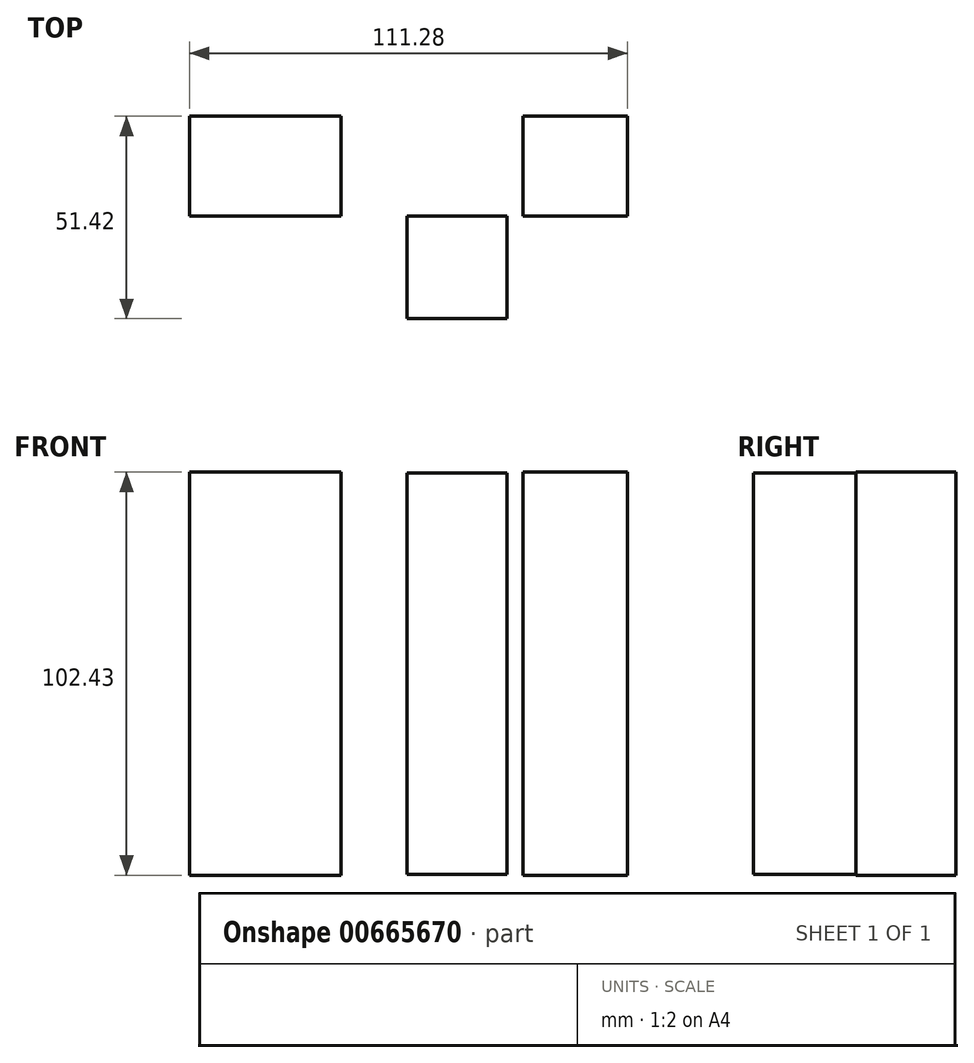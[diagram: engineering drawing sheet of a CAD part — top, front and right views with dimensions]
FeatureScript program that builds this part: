
annotation { "Feature Type Name" : "Feature", "Feature Type Description" : "" }
export const myFeature = defineFeature(function(context is Context, id is Id, definition is map)
    precondition{}
    {
        {
            var Q0;
            Q0=qCreatedBy(makeId("Front.planeOp"),FACE);
            var sketch = newSketch(context, id + "F0", { "sketchPlane" : qUnion([Q0])});
            skLineSegment(sketch, "E0", {"start": v(-55.23, 46.38) * mm, "end": v(-55.23, -56.05) * mm});
            skLineSegment(sketch, "E1", {"start": v(-55.23, -56.05) * mm, "end": v(56.05, -56.05) * mm});
            skLineSegment(sketch, "E2", {"start": v(56.05, -56.05) * mm, "end": v(56.05, 46.38) * mm});
            skLineSegment(sketch, "E3", {"start": v(56.05, 46.38) * mm, "end": v(-55.23, 46.38) * mm});
            skSolve(sketch);
        }
        {
            var Q0;
            Q0 = qSketchRegion(id + "F0", true);
            extrude(context, id + "F1", {"entities" : qUnion([Q0]), "oppositeDirection" : true, "depth" : 25.4 * mm, "offsetDistance" : 25.4 * mm});
        }
        {
            var Q0;
            Q0=qCreatedBy(makeId("Right.planeOp"),FACE);
            var sketch = newSketch(context, id + "F2", { "sketchPlane" : qUnion([Q0])});
            skLineSegment(sketch, "E4", {"start": v(0, 46.18) * mm, "end": v(-26.02, 46.18) * mm});
            skLineSegment(sketch, "E5", {"start": v(-26.02, 46.18) * mm, "end": v(-26.02, -55.84) * mm});
            skLineSegment(sketch, "E6", {"start": v(-26.02, -55.84) * mm, "end": v(0, -55.84) * mm});
            skLineSegment(sketch, "E7", {"start": v(0, -55.84) * mm, "end": v(0, 46.18) * mm});
            skSolve(sketch);
        }
        {
            var Q0;
            Q0 = qSketchRegion(id + "F2", true);
            extrude(context, id + "F3", {"entities" : qUnion([Q0]), "operationType" : NewBodyOperationType.ADD, "depth" : 25.4 * mm, "offsetDistance" : 25.4 * mm});
        }
        {
            var Q0;
            Q0=makeQuery(id+"F1.opExtrude","CAP_FACE",FACE,{"disambiguationData":[OSD([sQuery(id+"F0.wireOp",EDGE,"E0"),sQuery(id+"F0.wireOp",EDGE,"E1"),sQuery(id+"F0.wireOp",EDGE,"E2"),sQuery(id+"F0.wireOp",EDGE,"E3")])],"isStart":false});
            var sketch = newSketch(context, id + "F4", { "sketchPlane" : qUnion([Q0])});
            skLineSegment(sketch, "E8.bottom", {"start": v(-9.15, -56.05) * mm, "end": v(16.76, -56.05) * mm});
            skLineSegment(sketch, "E8.top", {"start": v(-9.15, 46.38) * mm, "end": v(16.76, 46.38) * mm});
            skLineSegment(sketch, "E8.left", {"start": v(-9.15, -56.05) * mm, "end": v(-9.15, 46.38) * mm});
            skLineSegment(sketch, "E8.right", {"start": v(16.76, -56.05) * mm, "end": v(16.76, 46.38) * mm});
            skLineSegment(sketch, "E9.bottom", {"start": v(-9.15, 43.7) * mm, "end": v(-29.52, 43.7) * mm});
            skLineSegment(sketch, "E9.top", {"start": v(-9.15, -56.05) * mm, "end": v(-29.52, -56.05) * mm});
            skLineSegment(sketch, "E9.left", {"start": v(-9.15, 43.7) * mm, "end": v(-9.15, -56.05) * mm});
            skLineSegment(sketch, "E9.right", {"start": v(-29.52, 43.7) * mm, "end": v(-29.52, -56.05) * mm});
            skLineSegment(sketch, "E10.bottom", {"start": v(-29.52, 43.7) * mm, "end": v(-29.52, 43.7) * mm});
            skLineSegment(sketch, "E10.top", {"start": v(-29.52, 46.38) * mm, "end": v(-29.52, 46.38) * mm});
            skLineSegment(sketch, "E10.left", {"start": v(-29.52, 43.7) * mm, "end": v(-29.52, 46.38) * mm});
            skLineSegment(sketch, "E10.right", {"start": v(-29.52, 43.7) * mm, "end": v(-29.52, 46.38) * mm});
            skLineSegment(sketch, "E11.bottom", {"start": v(-29.52, 46.38) * mm, "end": v(16.76, 46.38) * mm});
            skLineSegment(sketch, "E11.top", {"start": v(-29.52, 43.7) * mm, "end": v(16.76, 43.7) * mm});
            skLineSegment(sketch, "E11.left", {"start": v(-29.52, 46.38) * mm, "end": v(-29.52, 43.7) * mm});
            skLineSegment(sketch, "E11.right", {"start": v(16.76, 46.38) * mm, "end": v(16.76, 43.7) * mm});
            skLineSegment(sketch, "E12.bottom", {"start": v(16.76, 43.7) * mm, "end": v(-29.52, 43.7) * mm});
            skLineSegment(sketch, "E12.top", {"start": v(16.76, 21.08) * mm, "end": v(-29.52, 21.08) * mm});
            skLineSegment(sketch, "E12.left", {"start": v(16.76, 43.7) * mm, "end": v(16.76, 21.08) * mm});
            skLineSegment(sketch, "E12.right", {"start": v(-29.52, 43.7) * mm, "end": v(-29.52, 21.08) * mm});
            skSolve(sketch);
        }
        {
            var Q0;
            Q0 = qSketchRegion(id + "F4", true);
            extrude(context, id + "F5", {"entities" : qUnion([Q0]), "operationType" : NewBodyOperationType.REMOVE, "oppositeDirection" : true, "depth" : 25.4 * mm, "offsetDistance" : 25.4 * mm});
        }
    });
